# Revit family: Furniture_Chairs_Stools_Benches_Hags_Curved_bench_Sofiero_situ_O_800
name_source: partatom
category: Furniture
revit_build: Autodesk Revit 2018 (Build: 20190510_1515(x64)
units: mm (PartAtom-declared; Revit-internal decimal feet)

## family parameters
Always vertical = Yes
Cut with Voids When Loaded = No
OmniClass Number = 23.11.27.00
OmniClass Title = Landscaping
Room Calculation Point = No
Shared = No
Work Plane-Based = No

## types (2) — shared parameters
BIMobject category = Chairs, Stools & Benches
Description = Sofiero Curved bench Ø 800
Edition number = 1
IFC Classification = Furniture
Manufacturer = Hags
Manufacturer name = HAGS
Masterformat 2014 Code = 12 50 00
Masterformat 2014 Description = Furniture
OmniClass Code = 23-21 25 19 11 13
OmniClass Description = Benches
Product Guid = 567f0998-0523-47ae-929d-07faabcaab01
Product SKU = Curved_bench_Sofiero_situ_O_800
Product data url = https://bimobject.com
Product name = Sofiero Curved bench Ø 800
Product url = https://hags.se
QR code = https://bimobject.com
URL = https://www.hags.com
Uniclass 1.4 Code = JN
Uniclass 1.4 Description = Furniture/Equipment

## per-type parameters (varying)
| type | Body material | Construction material | Model |
| 8073169 Tan / Galv 90 ° | Hags - Wood - Tan | Hags - Steel - Galvanized | 8073169 |
| 8073700 Bark Brown / Black 90 ° | Hags - Wood - Bark brown | Hags - Steel - Powder coated - Black | 8073700 |

## geometry (parser evidence)
native form markers: Sweep x2
no freeform markers — native parametric forms only
